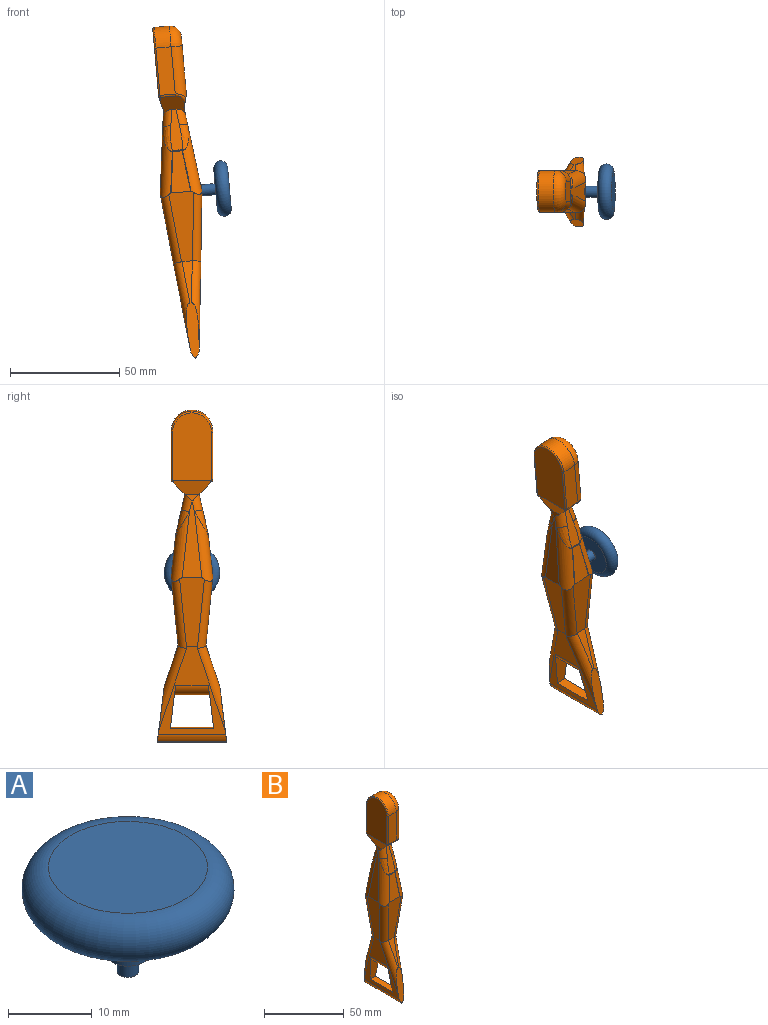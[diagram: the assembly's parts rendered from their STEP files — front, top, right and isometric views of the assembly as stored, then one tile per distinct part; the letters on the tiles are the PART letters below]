
ASSEMBLY  parts=2 mates=1
PART A: 7 faces, bbox 27.5x27.5x15.2 mm
  f0: plane 19.05x19.05mm, normal (0,0,1), area 285mm2, adj f1
  f1: torus R=9.53mm, axis (0,0,-1), area 723.6mm2, adj f0,f2
  f2: plane 19.05x19.05mm, normal (0,0,-1), area 264.8mm2, adj f1,f3
  f3: cylinder r=2.54mm len=6.35mm, axis (0,0,-1), area 101.3mm2, adj f2,f4
  f4: plane 5.08x5.08mm, normal (0,0,-1), area 15.2mm2, adj f3,f5
  f5: cylinder r=1.27mm len=2.54mm, axis (0,0,1), area 20.3mm2, adj f4,f6
  f6: plane 2.54x2.54mm, normal (0,0,-1), area 5.1mm2, adj f5
PART B: 85 faces, bbox 20.4x38.5x154 mm
  f0: plane 41.75x31.64mm, normal (0.99,0,-0.11), area 400.3mm2, adj f2,f5,f16,f32,f36,f53,f55,f69
  f1: plane 41.75x31.64mm, normal (-0.99,0,-0.11), area 400.3mm2, adj f5,f16,f19,f30,f34,f52,f54,f70
  f2: plane 32.26x11.86mm, normal (1,0,-0.1), area 253.9mm2, adj f0,f3,f32,f36,f44,f51,f72
  f3: plane 39.24x9.6mm, normal (0.99,0,0.12), area 176.8mm2, adj f2,f9,f14,f21,f33,f37,f44,f51
  f4: plane 19.05x6.35mm, normal (0,-0.95,0.32), area 55mm2, adj f5,f15,f52,f53
  f5: plane 25.44x5.44mm, normal (0,-0.99,0.12), area 113.2mm2, adj f0,f1,f4,f25,f26,f52,f53,f67
  f6: plane 21.7x6.99mm, normal (0,-1,0), area 151.6mm2, adj f8,f27,f56,f62
  f7: plane 21.7x6.99mm, normal (0,1,0), area 151.6mm2, adj f8,f29,f58,f64
  f8: cylinder r=9.53mm len=19.05mm, axis (-1,0,0), area 209mm2, adj f6,f7,f28,f63
  f9: plane 11.7x9.92mm, normal (0,-0.71,-0.71), area 90.7mm2, adj f3,f10,f23,f24,f31,f33,f56,f57
  f10: plane 18.78x5.21mm, normal (0,-0.98,0.22), area 78.6mm2, adj f9,f31,f33,f46,f48,f50
  f11: plane 18.78x8.95mm, normal (0,-0.99,0.11), area 124.8mm2, adj f15,f45,f48,f51
  f12: plane 18.78x8.95mm, normal (0,0.99,0.11), area 124.7mm2, adj f18,f39,f41,f44
  f13: plane 18.78x5.21mm, normal (0,0.98,0.22), area 78.6mm2, adj f14,f35,f37,f38,f41,f42
  f14: plane 11.7x9.92mm, normal (0,0.71,-0.71), area 90.7mm2, adj f3,f13,f23,f24,f35,f37,f58,f59
  f15: plane 32.05x11.64mm, normal (0,-1,-0.1), area 264.1mm2, adj f4,f11,f30,f32,f45,f51,f52,f53
  f16: plane 25.44x5.44mm, normal (0,0.99,0.12), area 113.2mm2, adj f0,f1,f17,f25,f26,f54,f55,f67
  f17: plane 19.05x6.35mm, normal (0,0.95,0.32), area 55mm2, adj f16,f18,f54,f55
  f18: plane 32.05x11.64mm, normal (0,1,-0.1), area 264.1mm2, adj f12,f17,f34,f36,f39,f44,f54,f55
  f19: plane 32.03x11.63mm, normal (-1,0,-0.1), area 264.1mm2, adj f1,f23,f30,f34,f39,f45
  f20: plane 26.67x8.89mm, normal (1,0,0), area 228.6mm2, adj f21,f27,f28,f29
  f21: plane 14.04x7.21mm, normal (0.97,0,-0.24), area 70.9mm2, adj f3,f20,f27,f29,f57,f59
  f22: plane 31.12x17.78mm, normal (-1,0,0), area 519.2mm2, adj f24,f60,f61,f62,f63,f64,f65,f66
  f23: plane 38.1x8.97mm, normal (-0.99,0,0.12), area 187mm2, adj f9,f14,f19,f24,f31,f35,f39,f45
  f24: plane 17.56x6.35mm, normal (-0.97,0,-0.24), area 82.1mm2, adj f9,f14,f22,f23,f60,f65
  f25: plane 31.73x0.17mm, normal (-0.67,0,-0.74), area 7.1mm2, adj f5,f16,f68,f70
  f26: plane 31.73x0.17mm, normal (0.67,0,-0.74), area 7.1mm2, adj f5,f16,f67,f69
  f27: cylinder r=5.08mm len=23.97mm, axis (0,0,-1), area 182.8mm2, adj f6,f20,f21,f28,f57
  f28: torus R=4.45mm, axis (1,0,0), area 192.5mm2, adj f8,f20,f27,f29
  f29: cylinder r=5.08mm len=23.97mm, axis (0,0,-1), area 182.8mm2, adj f7,f20,f21,f28,f59
  f30: cylinder r=3.81mm len=32.8mm, axis (0.1,0.1,-0.99), area 185.3mm2, adj f1,f15,f19,f45,f52
  f31: cylinder r=3.81mm len=7.98mm, axis (-0.12,-0.22,-0.97), area 37.2mm2, adj f9,f10,f23,f46
  f32: cylinder r=3.81mm len=32.8mm, axis (0.1,-0.1,0.99), area 185.3mm2, adj f0,f2,f15,f51,f53
  f33: cylinder r=3.81mm len=7.98mm, axis (-0.12,0.22,0.97), area 37.2mm2, adj f3,f9,f10,f50
  f34: cylinder r=3.81mm len=32.8mm, axis (-0.1,0.1,0.99), area 185.3mm2, adj f1,f18,f19,f39,f54
  f35: cylinder r=3.81mm len=8.06mm, axis (0.12,-0.22,0.97), area 37.8mm2, adj f13,f14,f23,f38
  f36: cylinder r=3.81mm len=32.8mm, axis (-0.1,-0.1,-0.99), area 185.3mm2, adj f0,f2,f18,f44,f55
  f37: cylinder r=3.81mm len=8.06mm, axis (0.12,0.22,-0.97), area 37.8mm2, adj f3,f13,f14,f42
  f38: bspline ~12.95x6.74mm, area 44.8mm2, adj f13,f35,f39,f40
  f39: cylinder r=5.08mm len=32.31mm, axis (-0.12,0.11,-0.99), area 193.4mm2, adj f12,f18,f19,f23,f34,f38,f40
  f40: bspline ~1.13x1.11mm, area 0.1mm2, adj f38,f39,f41
  f41: cylinder r=5.08mm len=4.5mm, axis (-1,0,0), area 2.4mm2, adj f12,f13,f40,f43
  f42: bspline ~12.95x6.74mm, area 44.8mm2, adj f13,f37,f43,f44
  f43: bspline ~1.13x1.11mm, area 0.1mm2, adj f41,f42,f44
  f44: cylinder r=5.08mm len=32.31mm, axis (0.12,0.11,-0.99), area 193.4mm2, adj f2,f3,f12,f18,f36,f42,f43
  f45: cylinder r=5.08mm len=32.4mm, axis (0.12,0.11,0.99), area 193.7mm2, adj f11,f15,f19,f23,f30,f46,f47
  f46: bspline ~13.07x6.76mm, area 45.2mm2, adj f10,f31,f45,f47
  f47: bspline ~1.13x1.11mm, area 0.1mm2, adj f45,f46,f48
  f48: cylinder r=5.08mm len=4.5mm, axis (-1,0,0), area 2.4mm2, adj f10,f11,f47,f49
  f49: bspline ~1.13x1.11mm, area 0.1mm2, adj f48,f50,f51
  f50: bspline ~13.07x6.76mm, area 45.2mm2, adj f10,f33,f49,f51
  f51: cylinder r=5.08mm len=32.4mm, axis (-0.12,0.11,0.99), area 193.7mm2, adj f2,f3,f11,f15,f32,f49,f50
  f52: cylinder r=3.81mm len=39.55mm, axis (0.1,-0.31,-0.94), area 167.6mm2, adj f1,f4,f5,f15,f30
  f53: cylinder r=3.81mm len=39.55mm, axis (0.1,0.31,0.94), area 167.6mm2, adj f0,f4,f5,f15,f32
  f54: cylinder r=3.81mm len=39.55mm, axis (-0.1,-0.31,0.94), area 167.6mm2, adj f1,f16,f17,f18,f34
  f55: cylinder r=3.81mm len=39.55mm, axis (-0.1,0.31,-0.94), area 167.6mm2, adj f0,f16,f17,f18,f36
  f56: cylinder r=1.27mm len=6.99mm, axis (1,0,0), area 7mm2, adj f6,f9,f57,f61
  f57: bspline ~8.35x7.89mm, area 9.1mm2, adj f3,f9,f21,f27,f56
  f58: cylinder r=1.27mm len=6.99mm, axis (1,0,0), area 7mm2, adj f7,f14,f59,f66
  f59: bspline ~8.35x7.89mm, area 9.1mm2, adj f3,f14,f21,f29,f58
  f60: cylinder r=0.64mm len=2.62mm, axis (0,0.71,-0.71), area 1mm2, adj f9,f22,f24,f61
  f61: torus R=0.64mm, axis (1,0,0), area 0.8mm2, adj f22,f56,f60,f62
  f62: cylinder r=0.64mm len=21.7mm, axis (0,0,1), area 21.6mm2, adj f6,f22,f61,f63
  f63: torus R=8.89mm, axis (1,0,0), area 29.1mm2, adj f8,f22,f62,f64
  f64: cylinder r=0.64mm len=21.7mm, axis (0,0,1), area 21.6mm2, adj f7,f22,f63,f66
  f65: cylinder r=0.64mm len=2.62mm, axis (0,-0.71,-0.71), area 1mm2, adj f14,f22,f24,f66
  f66: torus R=0.64mm, axis (1,0,0), area 0.8mm2, adj f22,f58,f64,f65
  f67: cylinder r=0.25mm len=31.75mm, axis (0,-1,0), area 4.8mm2, adj f5,f16,f26,f68
  f68: cylinder r=0.25mm len=31.75mm, axis (0,-1,0), area 4.8mm2, adj f5,f16,f25,f67
  f69: cylinder r=5.08mm len=31.7mm, axis (0,-1,0), area 116.4mm2, adj f0,f5,f16,f26
  f70: cylinder r=5.08mm len=31.7mm, axis (0,1,0), area 116.4mm2, adj f1,f5,f16,f25
  f71: cylinder r=1.52mm len=3.05mm, axis (-1,0,0), area 0mm2, adj f73,f83
  f72: cylinder r=2.54mm len=5.08mm, axis (-1,0,0), area 0mm2, adj f2,f73
  f73: plane 5.08x5.08mm, normal (1,0,0), area 13mm2, adj f71,f72,f74,f75
  f74: cylinder r=1.52mm len=3.05mm, axis (-1,0,0), area 0mm2, adj f73,f81
  f75: cylinder r=2.54mm len=5.08mm, axis (-1,0,0), area 0mm2, adj f3,f73
  f76: plane 19.85x8.99mm, normal (0,0.99,-0.12), area 103.2mm2, adj f0,f1,f77,f79,f80
  f77: plane 19.87x4.58mm, normal (0,0,1), area 91mm2, adj f0,f1,f76,f78
  f78: plane 19.85x8.99mm, normal (0,-0.99,-0.12), area 103.2mm2, adj f0,f1,f77,f79,f80
  f79: cylinder r=5.08mm len=16.08mm, axis (0,-1,0), area 105.2mm2, adj f1,f76,f78,f80
  f80: cylinder r=5.08mm len=16.08mm, axis (0,1,0), area 105.2mm2, adj f0,f76,f78,f79
  f81: extruded ~5.25x3.05mm, area 24.1mm2, adj f74,f82,f83
  f82: plane 3.05x1.52mm, normal (0.99,0,0.12), area 3.7mm2, adj f81,f84
  f83: extruded ~5.21x3.05mm, area 24.4mm2, adj f71,f81,f84
  f84: plane 3.05x1.52mm, normal (1,0,-0.1), area 3.7mm2, adj f82,f83
PLACE A rot(axis=(0.68,0,0.74),180deg) t=(-8.91,4.47,21.59)mm
PLACE B rot(axis=(0,-1,0),5deg) t=(-27.89,4.47,19.93)mm
MATE fastened A.f1 <-> B.f72  axis (-1,0,-0.09) through (-8.91,4.47,21.59)mm
